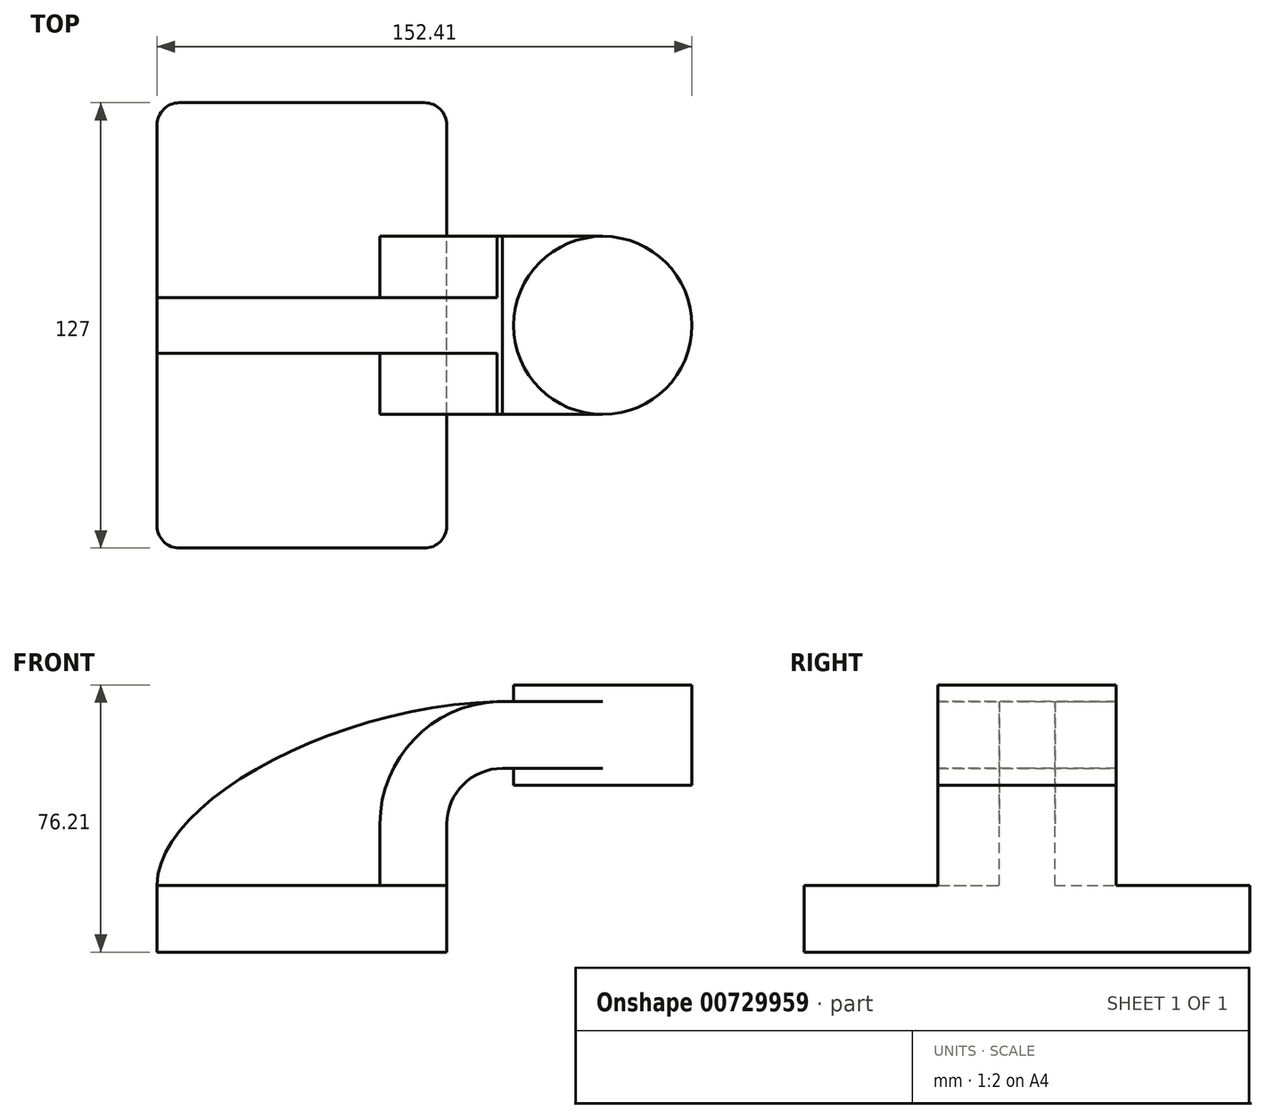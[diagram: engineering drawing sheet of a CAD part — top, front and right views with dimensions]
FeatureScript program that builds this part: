
annotation { "Feature Type Name" : "Feature", "Feature Type Description" : "" }
export const myFeature = defineFeature(function(context is Context, id is Id, definition is map)
    precondition{}
    {
        {
            var Q0;
            Q0=qCreatedBy(makeId("Front.planeOp"),FACE);
            var sketch = newSketch(context, id + "F0", { "sketchPlane" : qUnion([Q0])});
            skLineSegment(sketch, "E0.bottom", {"start": v(-41.28, 9.52) * mm, "end": v(41.28, 9.53) * mm});
            skLineSegment(sketch, "E0.top", {"start": v(-41.28, -9.53) * mm, "end": v(41.28, -9.53) * mm});
            skLineSegment(sketch, "E0.left", {"start": v(-41.28, 9.52) * mm, "end": v(-41.28, -9.53) * mm});
            skLineSegment(sketch, "E0.right", {"start": v(41.28, 9.53) * mm, "end": v(41.28, -9.52) * mm});
            skPoint(sketch, "E0.middle", {"position": v(0, 0) * mm});
            skLineSegment(sketch, "E1.bottom", {"start": v(111.12, 38.1) * mm, "end": v(60.32, 38.1) * mm});
            skLineSegment(sketch, "E1.top", {"start": v(111.12, 66.68) * mm, "end": v(60.32, 66.68) * mm});
            skLineSegment(sketch, "E1.left", {"start": v(111.12, 38.1) * mm, "end": v(111.12, 66.68) * mm});
            skLineSegment(sketch, "E1.right", {"start": v(60.32, 38.1) * mm, "end": v(60.32, 66.67) * mm});
            skPoint(sketch, "E1.middle", {"position": v(85.72, 52.39) * mm});
            skLineSegment(sketch, "E2", {"start": v(41.27, 9.53) * mm, "end": v(41.27, 27) * mm});
            skArc(sketch, "E3", {"start": v(41.27, 27) * mm, "mid": v(45.92, 38.23) * mm, "end": v(57.15, 42.88) * mm});
            skLineSegment(sketch, "E4", {"start": v(57.15, 42.88) * mm, "end": v(85.72, 42.88) * mm});
            skLineSegment(sketch, "E5.0", {"start": v(57.15, 61.93) * mm, "end": v(85.72, 61.93) * mm});
            skArc(sketch, "E5.1", {"start": v(22.22, 27) * mm, "mid": v(32.45, 51.7) * mm, "end": v(57.15, 61.93) * mm});
            skLineSegment(sketch, "E5.2", {"start": v(22.22, 9.53) * mm, "end": v(22.22, 27) * mm});
            skLineSegment(sketch, "E6", {"start": v(85.72, 38.1) * mm, "end": v(85.72, 66.68) * mm});
            skFitSpline(sketch, "E7", {"points": [v(-41.28, 9.52) * mm, v(57.15, 61.93) * mm], "startDerivative": vector(-0.5, 70.78) * mm, "endDerivative": vector(143.5, 2.25) * mm});
            skSolve(sketch);
        }
        {
            var Q0;
            Q0=makeQuery(id+"F0.imprint","IMPRINT",FACE,{"disambiguationData":[TD([[makeQuery(id+"F0.imprint","IMPRINT",EDGE,{"derivedFrom":sQuery(id+"F0.wireOp",EDGE,"E0.top")}),1.0]])]});
            extrude(context, id + "F1", {"entities" : qUnion([Q0]), "endBound" : BoundingType.SYMMETRIC, "depth" : 127 * mm, "offsetDistance" : 25.4 * mm});
        }
        {
            var Q0;
            {var subQ1=sQuery(id+"F0.wireOp",EDGE,"E2");Q0=makeQuery(id+"F0.imprint","IMPRINT",FACE,{"disambiguationData":[TD([[makeQuery(id+"F0.imprint","IMPRINT",EDGE,{"derivedFrom":subQ1}),1.0]])]});}
            var Q1;
            {var subQ0=sQuery(id+"F0.wireOp",EDGE,"E4");var subQ1=sQuery(id+"F0.wireOp",EDGE,"E1.right");var subQ2=makeQuery(id+"F0.imprint","INTERSECT",VERTEX,{"derivedFrom":[subQ1,subQ0]});Q1=makeQuery(id+"F0.imprint","IMPRINT",FACE,{"disambiguationData":[TD([[makeQuery(id+"F0.imprint","IMPRINT",EDGE,{"disambiguationData":[TD([[subQ2,-1.0]])],"derivedFrom":subQ1}),-1.0]])]});}
            extrude(context, id + "F2", {"entities" : qUnion([Q0, Q1]), "operationType" : NewBodyOperationType.ADD, "endBound" : BoundingType.SYMMETRIC, "depth" : 50.8 * mm, "offsetDistance" : 25.4 * mm});
        }
        {
            var Q0;
            {var subQ3=sQuery(id+"F0.wireOp",EDGE,"E5.2");Q0=makeQuery(id+"F0.imprint","IMPRINT",FACE,{"disambiguationData":[TD([[makeQuery(id+"F0.imprint","IMPRINT",EDGE,{"derivedFrom":subQ3}),1.0]])]});}
            extrude(context, id + "F3", {"entities" : qUnion([Q0]), "operationType" : NewBodyOperationType.ADD, "endBound" : BoundingType.SYMMETRIC, "depth" : 15.88 * mm, "offsetDistance" : 25.4 * mm});
        }
        {
            var Q0;
            {var subQ0=sQuery(id+"F0.wireOp",EDGE,"E1.left");Q0=makeQuery(id+"F0.imprint","IMPRINT",FACE,{"disambiguationData":[TD([[makeQuery(id+"F0.imprint","IMPRINT",EDGE,{"derivedFrom":subQ0}),1.0]])]});}
            var Q1;
            Q1=sQuery(id+"F0.wireOp",EDGE,"E6");
            revolve(context, id + "F4", {"operationType" : NewBodyOperationType.ADD, "surfaceOperationType" : NewSurfaceOperationType.NEW, "entities" : qUnion([Q0]), "axis" : qUnion([Q1]), "revolveType" : RevolveType.FULL});
        }
        {
            var Q0;
            Q0=makeQuery(id+"F1.opExtrude","CAP_EDGE",EDGE,{"disambiguationData":[OSD([sQuery(id+"F0.wireOp",EDGE,"E0.left")])],"isStart":false});
            var Q1;
            Q1=makeQuery(id+"F1.opExtrude","CAP_EDGE",EDGE,{"disambiguationData":[OSD([sQuery(id+"F0.wireOp",EDGE,"E0.right")])],"isStart":false});
            var Q2;
            Q2=makeQuery(id+"F1.opExtrude","CAP_EDGE",EDGE,{"disambiguationData":[OSD([sQuery(id+"F0.wireOp",EDGE,"E0.left")])],"isStart":true});
            var Q3;
            Q3=makeQuery(id+"F1.opExtrude","CAP_EDGE",EDGE,{"disambiguationData":[OSD([sQuery(id+"F0.wireOp",EDGE,"E0.right")])],"isStart":true});
            fillet(context, id + "F5", {"entities" : qUnion([Q0, Q1, Q2, Q3]), "radius" : 6.35 * mm, "tangentPropagation" : true, "allowEdgeOverflow" : false});
        }
    });
